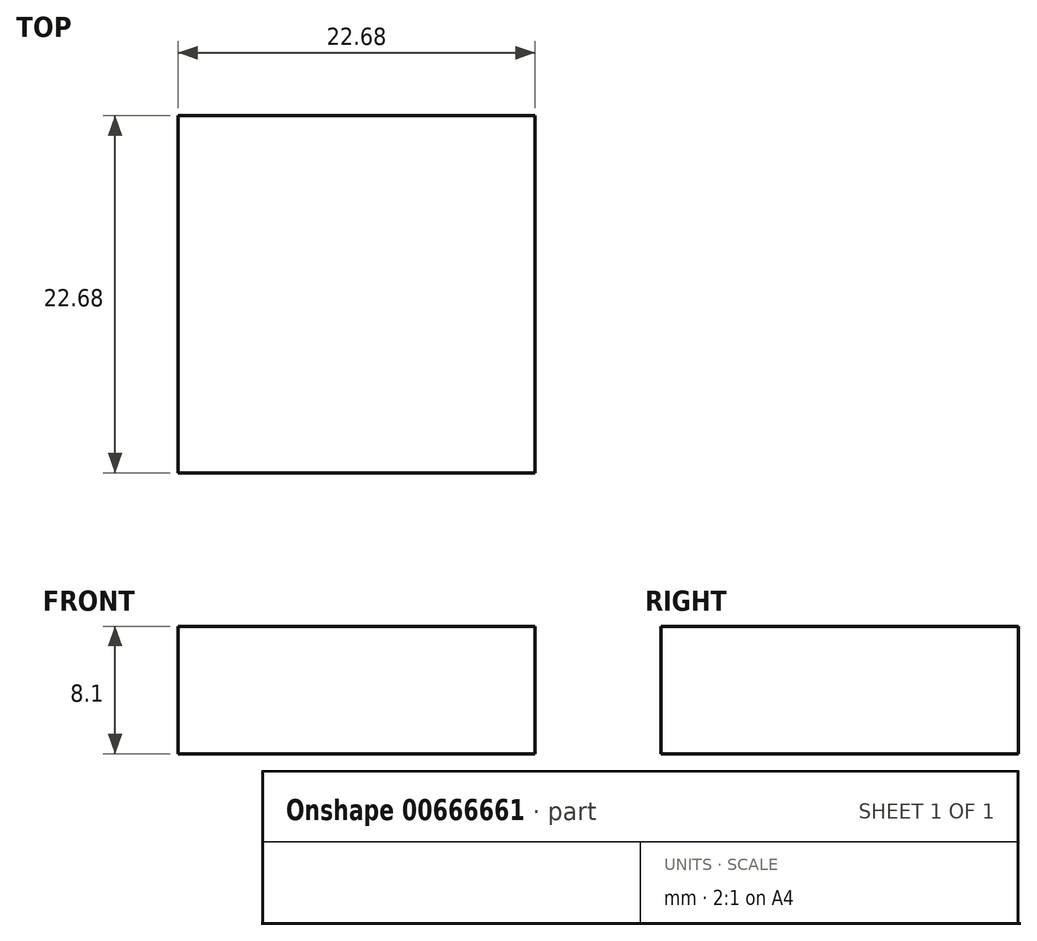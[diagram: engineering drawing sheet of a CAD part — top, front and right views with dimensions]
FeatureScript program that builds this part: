
annotation { "Feature Type Name" : "Feature", "Feature Type Description" : "" }
export const myFeature = defineFeature(function(context is Context, id is Id, definition is map)
    precondition{}
    {
        {
            var Q0;
            Q0=qCreatedBy(makeId("Top.planeOp"),FACE);
            var sketch = newSketch(context, id + "F0", { "sketchPlane" : qUnion([Q0])});
            skLineSegment(sketch, "E0.bottom", {"start": v(-11.34, 11.34) * mm, "end": v(11.34, 11.34) * mm});
            skLineSegment(sketch, "E0.top", {"start": v(-11.34, -11.34) * mm, "end": v(11.34, -11.34) * mm});
            skLineSegment(sketch, "E0.left", {"start": v(-11.34, 11.34) * mm, "end": v(-11.34, -11.34) * mm});
            skLineSegment(sketch, "E0.right", {"start": v(11.34, 11.34) * mm, "end": v(11.34, -11.34) * mm});
            skSolve(sketch);
        }
        {
            var Q0;
            Q0=makeQuery(id+"F0.imprint","IMPRINT",FACE,{"disambiguationData":[TD([[makeQuery(id+"F0.imprint","IMPRINT",EDGE,{"derivedFrom":sQuery(id+"F0.wireOp",EDGE,"E0.bottom")}),-1.0]])]});
            extrude(context, id + "F1", {"entities" : qUnion([Q0]), "depth" : 8.1 * mm, "offsetDistance" : 25 * mm});
        }
    });
